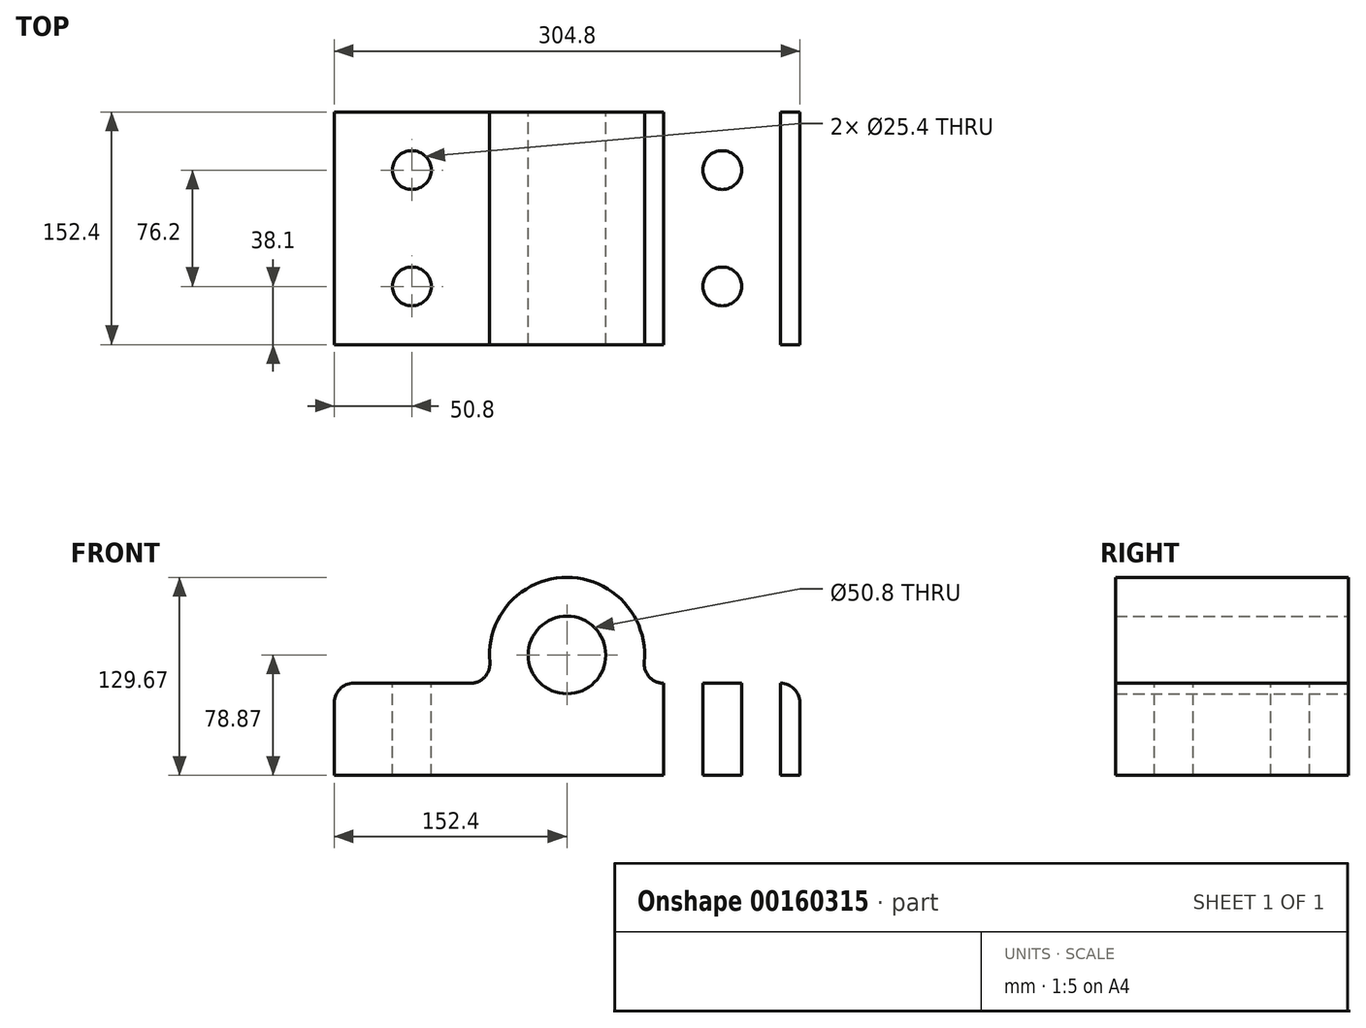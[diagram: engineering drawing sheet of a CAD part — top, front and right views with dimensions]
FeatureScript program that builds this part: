
annotation { "Feature Type Name" : "Feature", "Feature Type Description" : "" }
export const myFeature = defineFeature(function(context is Context, id is Id, definition is map)
    precondition{}
    {
        {
            var Q0;
            Q0=qCreatedBy(makeId("Front.planeOp"),FACE);
            var sketch = newSketch(context, id + "F0", { "sketchPlane" : qUnion([Q0])});
            skCircle(sketch, "E0", {"center": v(0, 0) * mm, "radius": 25.4 * mm});
            skLineSegment(sketch, "E1", {"start": v(-63.23, -18.53) * mm, "end": v(-139.7, -18.53) * mm});
            skLineSegment(sketch, "E2", {"start": v(-152.4, -31.23) * mm, "end": v(-152.4, -78.87) * mm});
            skLineSegment(sketch, "E3", {"start": v(-152.4, -78.87) * mm, "end": v(152.4, -78.87) * mm});
            skLineSegment(sketch, "E4", {"start": v(152.4, -78.87) * mm, "end": v(152.4, -31.23) * mm});
            skLineSegment(sketch, "E5", {"start": v(139.7, -18.53) * mm, "end": v(63.23, -18.53) * mm});
            skPoint(sketch, "E6.visualSharp", {"position": v(152.4, -18.53) * mm});
            skArc(sketch, "E6.filletArc", {"start": v(152.4, -31.23) * mm, "mid": v(148.68, -22.25) * mm, "end": v(139.7, -18.53) * mm});
            skPoint(sketch, "E7.visualSharp", {"position": v(-152.4, -18.53) * mm});
            skArc(sketch, "E7.filletArc", {"start": v(-139.7, -18.53) * mm, "mid": v(-148.68, -22.25) * mm, "end": v(-152.4, -31.23) * mm});
            skPoint(sketch, "E8.visualSharp", {"position": v(47.3, -18.53) * mm});
            skArc(sketch, "E8.filletArc", {"start": v(50.59, -4.66) * mm, "mid": v(53.85, -14.39) * mm, "end": v(63.23, -18.53) * mm});
            skPoint(sketch, "E9.visualSharp", {"position": v(-47.3, -18.53) * mm});
            skArc(sketch, "E9.filletArc", {"start": v(-63.23, -18.53) * mm, "mid": v(-53.85, -14.39) * mm, "end": v(-50.59, -4.66) * mm});
            skCircle(sketch, "E10", {"center": v(0, 0) * mm, "radius": 50.8 * mm});
            skSolve(sketch);
        }
        {
            var Q0;
            Q0 = qSketchRegion(id + "F0", true);
            extrude(context, id + "F1", {"entities" : qUnion([Q0]), "depth" : 152.4 * mm});
        }
        {
            var Q0;
            Q0=makeQuery(id+"F1.opExtrude","SWEPT_FACE",FACE,{"disambiguationData":[OSD([sQuery(id+"F0.wireOp",EDGE,"E1")])]});
            var sketch = newSketch(context, id + "F2", { "sketchPlane" : qUnion([Q0])});
            skCircle(sketch, "E11", {"center": v(-101.6, -38.1) * mm, "radius": 12.7 * mm});
            skCircle(sketch, "E12", {"center": v(-101.6, -114.3) * mm, "radius": 12.7 * mm});
            skLineSegment(sketch, "E13.0.0", {"start": v(-63.23, 0) * mm, "end": v(-139.7, 0) * mm});
            skLineSegment(sketch, "E13.0.1", {"start": v(-139.7, 0) * mm, "end": v(-139.7, -152.4) * mm});
            skLineSegment(sketch, "E13.0.2", {"start": v(-139.7, -152.4) * mm, "end": v(-63.23, -152.4) * mm});
            skLineSegment(sketch, "E13.0.3", {"start": v(-63.23, -152.4) * mm, "end": v(-63.23, 0) * mm});
            skLineSegment(sketch, "E14.0.0", {"start": v(139.7, 0) * mm, "end": v(63.23, 0) * mm});
            skLineSegment(sketch, "E14.0.1", {"start": v(63.23, 0) * mm, "end": v(63.23, -152.4) * mm});
            skLineSegment(sketch, "E14.0.2", {"start": v(63.23, -152.4) * mm, "end": v(139.7, -152.4) * mm});
            skLineSegment(sketch, "E14.0.3", {"start": v(139.7, -152.4) * mm, "end": v(139.7, 0) * mm});
            skLineSegment(sketch, "E15", {"start": v(0, 0) * mm, "end": v(0, -164.4) * mm, "construction": true});
            skCircle(sketch, "E16.MirrorC", {"center": v(101.6, -38.1) * mm, "radius": 12.7 * mm});
            skCircle(sketch, "E17.MirrorC", {"center": v(101.6, -114.3) * mm, "radius": 12.7 * mm});
            skSolve(sketch);
        }
        {
            var Q0;
            Q0=makeQuery(id+"F2.imprint","IMPRINT",FACE,{"disambiguationData":[TD([[makeQuery(id+"F2.imprint","IMPRINT",EDGE,{"derivedFrom":sQuery(id+"F2.wireOp",EDGE,"E11")}),1.0]])]});
            var Q1;
            Q1=makeQuery(id+"F2.imprint","IMPRINT",FACE,{"disambiguationData":[TD([[makeQuery(id+"F2.imprint","IMPRINT",EDGE,{"derivedFrom":sQuery(id+"F2.wireOp",EDGE,"E12")}),1.0]])]});
            var Q2;
            Q2=makeQuery(id+"F2.imprint","IMPRINT",FACE,{"disambiguationData":[TD([[makeQuery(id+"F2.imprint","IMPRINT",EDGE,{"derivedFrom":sQuery(id+"F2.wireOp",EDGE,"E17.MirrorC")}),-1.0]])]});
            var Q3;
            Q3=makeQuery(id+"F2.imprint","IMPRINT",FACE,{"disambiguationData":[TD([[makeQuery(id+"F2.imprint","IMPRINT",EDGE,{"derivedFrom":sQuery(id+"F2.wireOp",EDGE,"E16.MirrorC")}),-1.0]])]});
            extrude(context, id + "F3", {"entities" : qUnion([Q0, Q1, Q2, Q3]), "operationType" : NewBodyOperationType.REMOVE, "endBound" : BoundingType.THROUGH_ALL, "oppositeDirection" : true, "depth" : 25.4 * mm});
        }
    });
